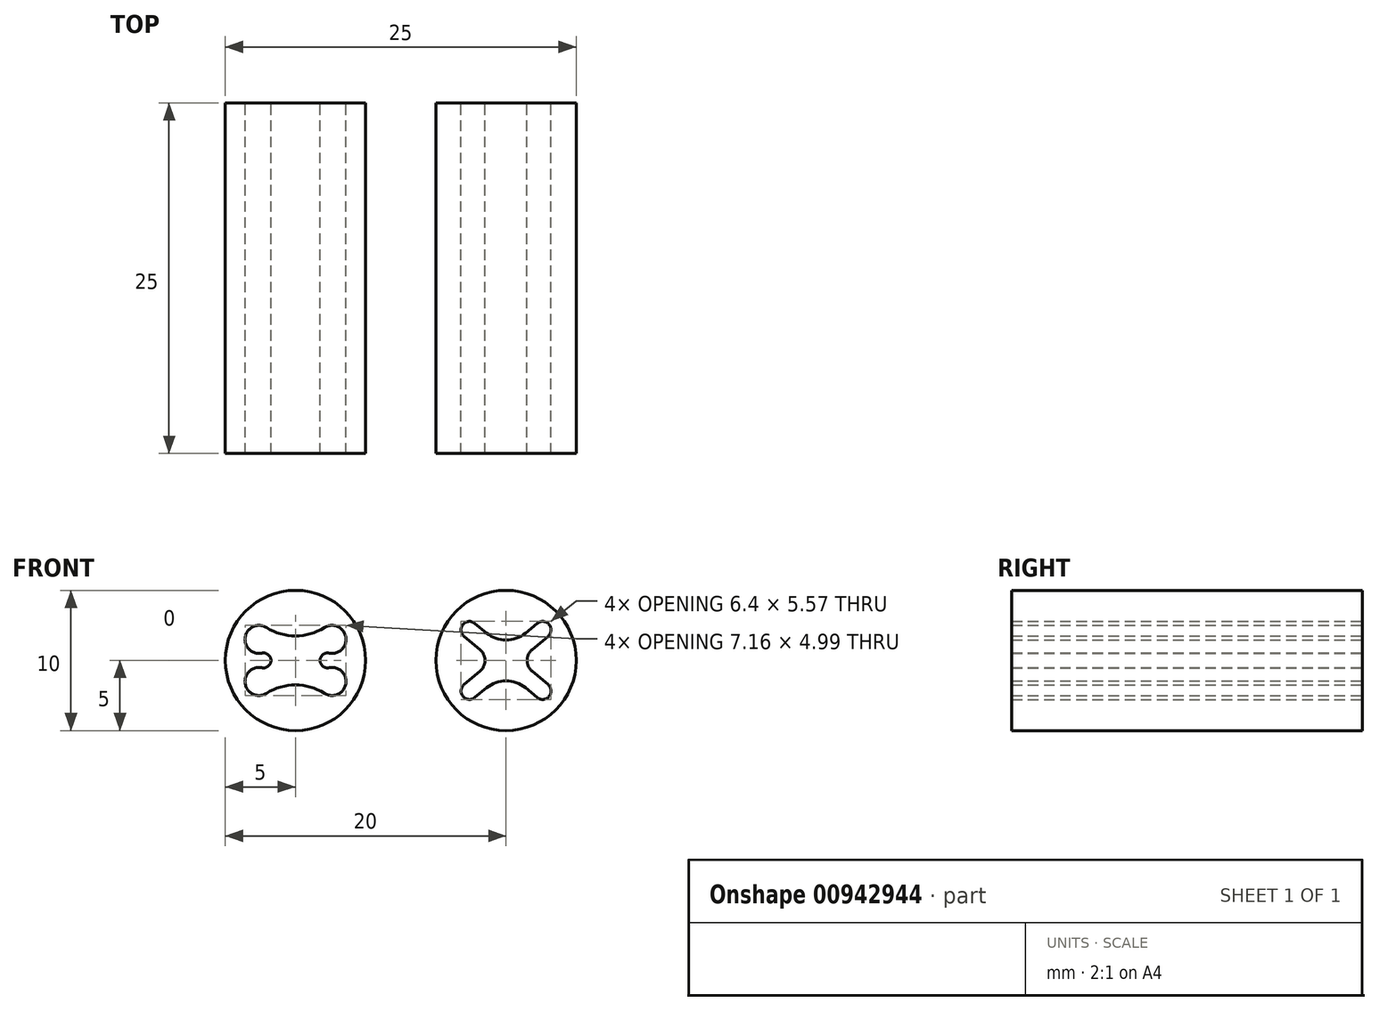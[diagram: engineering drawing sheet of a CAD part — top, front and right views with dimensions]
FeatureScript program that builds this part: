
annotation { "Feature Type Name" : "Feature", "Feature Type Description" : "" }
export const myFeature = defineFeature(function(context is Context, id is Id, definition is map)
    precondition{}
    {
        {
            var Q0;
            Q0=qCreatedBy(makeId("Front.planeOp"),FACE);
            var sketch = newSketch(context, id + "F0", { "sketchPlane" : qUnion([Q0])});
            skLineSegment(sketch, "E0", {"start": v(28.17, 0) * mm, "end": v(0, 0) * mm, "construction": true});
            skLineSegment(sketch, "E1", {"start": v(0, 0) * mm, "end": v(0, 19.38) * mm, "construction": true});
            skLineSegment(sketch, "E2", {"start": v(-34.44, -19.88) * mm, "end": v(0, 0) * mm, "construction": true});
            skCircle(sketch, "E3", {"center": v(0, 0) * mm, "radius": 4 * mm, "construction": true});
            skCircle(sketch, "E4", {"center": v(0, 0) * mm, "radius": 2.6 * mm, "construction": true});
            skArc(sketch, "E5", {"start": v(2.4, 0.52) * mm, "mid": v(3.58, 1.68) * mm, "end": v(2.07, 2.35) * mm});
            skArc(sketch, "E6.MirrorC", {"start": v(-2.4, 0.52) * mm, "mid": v(-3.58, 1.68) * mm, "end": v(-2.07, 2.35) * mm});
            skArc(sketch, "E7", {"start": v(-2.07, 2.35) * mm, "mid": v(0, 1.75) * mm, "end": v(2.07, 2.35) * mm});
            skArc(sketch, "E8.MirrorC", {"start": v(-2.4, -0.52) * mm, "mid": v(-3.58, -1.68) * mm, "end": v(-2.07, -2.35) * mm});
            skArc(sketch, "E9.MirrorCS", {"start": v(-2.07, -2.35) * mm, "mid": v(0, -1.75) * mm, "end": v(2.07, -2.35) * mm});
            skArc(sketch, "E10.MirrorC", {"start": v(2.4, -0.52) * mm, "mid": v(3.58, -1.68) * mm, "end": v(2.07, -2.35) * mm});
            skArc(sketch, "E11", {"start": v(-2.4, -0.52) * mm, "mid": v(-1.75, 0) * mm, "end": v(-2.4, 0.52) * mm});
            skArc(sketch, "E12.MirrorCS", {"start": v(2.4, -0.52) * mm, "mid": v(1.75, 0) * mm, "end": v(2.4, 0.52) * mm});
            skCircle(sketch, "E13", {"center": v(0, 0) * mm, "radius": 5 * mm});
            skPoint(sketch, "E14.start.orphan", {"position": v(80.44, 0) * mm});
            skPoint(sketch, "E15.orphan", {"position": v(40.22, 0) * mm});
            skLineSegment(sketch, "E16", {"start": v(15, 6.56) * mm, "end": v(15, 0) * mm, "construction": true});
            skCircle(sketch, "E17", {"center": v(15, 0) * mm, "radius": 5 * mm});
            skCircle(sketch, "E18", {"center": v(15, 0) * mm, "radius": 4 * mm, "construction": true});
            skCircle(sketch, "E19", {"center": v(15, 0) * mm, "radius": 2.6 * mm, "construction": true});
            skLineSegment(sketch, "E20", {"start": v(15, 0) * mm, "end": v(20.78, 4.85) * mm, "construction": true});
            skLineSegment(sketch, "E21", {"start": v(17.22, 2.65) * mm, "end": v(16.38, 1.95) * mm});
            skArc(sketch, "E22", {"start": v(18, 1.73) * mm, "mid": v(18.06, 2.57) * mm, "end": v(17.22, 2.65) * mm});
            skArc(sketch, "E23.MirrorC", {"start": v(12, 1.73) * mm, "mid": v(11.94, 2.57) * mm, "end": v(12.78, 2.65) * mm});
            skLineSegment(sketch, "E24.MirrorCS", {"start": v(12.78, 2.65) * mm, "end": v(13.62, 1.95) * mm});
            skArc(sketch, "E25", {"start": v(13.62, 1.95) * mm, "mid": v(15, 1.45) * mm, "end": v(16.38, 1.95) * mm});
            skLineSegment(sketch, "E26", {"start": v(16.85, 0.76) * mm, "end": v(18, 1.73) * mm});
            skLineSegment(sketch, "E27.MirrorCS", {"start": v(16.85, -0.76) * mm, "end": v(18, -1.73) * mm});
            skArc(sketch, "E28.MirrorC", {"start": v(18, -1.73) * mm, "mid": v(18.06, -2.57) * mm, "end": v(17.22, -2.65) * mm});
            skArc(sketch, "E29.MirrorC", {"start": v(12, -1.73) * mm, "mid": v(11.94, -2.57) * mm, "end": v(12.78, -2.65) * mm});
            skLineSegment(sketch, "E30.MirrorCS", {"start": v(12.78, -2.65) * mm, "end": v(13.62, -1.95) * mm});
            skArc(sketch, "E31.MirrorCS", {"start": v(13.62, -1.95) * mm, "mid": v(15, -1.45) * mm, "end": v(16.38, -1.95) * mm});
            skArc(sketch, "E32", {"start": v(16.85, 0.76) * mm, "mid": v(16.5, 0) * mm, "end": v(16.85, -0.76) * mm});
            skLineSegment(sketch, "E33.MirrorCS", {"start": v(17.22, -2.65) * mm, "end": v(16.38, -1.95) * mm});
            skLineSegment(sketch, "E34.MirrorCS", {"start": v(13.15, 0.76) * mm, "end": v(12, 1.73) * mm});
            skArc(sketch, "E35.MirrorCS", {"start": v(13.15, 0.76) * mm, "mid": v(13.5, 0) * mm, "end": v(13.15, -0.76) * mm});
            skLineSegment(sketch, "E36.MirrorCS", {"start": v(13.15, -0.76) * mm, "end": v(12, -1.73) * mm});
            skCircle(sketch, "E37", {"center": v(15, 0) * mm, "radius": 2 * mm, "construction": true});
            skSolve(sketch);
        }
        {
            var Q0;
            Q0 = qSketchRegion(id + "F0", true);
            extrude(context, id + "F1", {"entities" : qUnion([Q0]), "depth" : 25 * mm, "offsetDistance" : 25 * mm});
        }
    });
